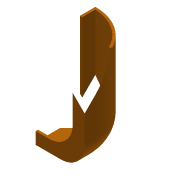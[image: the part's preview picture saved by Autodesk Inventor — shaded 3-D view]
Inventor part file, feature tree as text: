
AUTODESK INVENTOR PART (.ipt)
format: ipt  version: 2016 (Build 200138000, 138)  size: 146,432 bytes
history: native  units: mm
features: plane x4, sketch x3, extrude x3, reference x2, fillet x1, projected_geometry x1
ambient origin geometry x8: Origin, YZ Plane, XZ Plane, XY Plane, X Axis, Y Axis, Z Axis, Center Point
bodies: Body1 (feature_tree)
feature tree (14):
  sketch  "Sketch1"  dims[d1=2.0mm d2=2.0mm]
  plane  "Work Plane1"
  plane  "Work Plane2"
  plane  "Work Plane3"
  plane  "Work Plane4"
  extrude  "Extrusion2"  Depth=2.0mm
  extrude  "Extrusion3"  Depth=2.0mm
  extrude  "Extrusion4"  Depth=2.0mm TaperAngle=0.0deg
  fillet  "Fillet1"  Radius=8.0mm
  reference  "Reference1"
  reference  "Reference2"
  sketch  "Sketch2"  dims[d3=13.0mm d6=2.0mm]
  sketch  "Sketch3"  dims[d7=10.0mm d8=0.0mm d9=2.0mm d10=0.0mm d11=8.0mm d12=8.0mm d13=2.0mm d14=0.0mm d15=20.0mm]
  projected_geometry  "Projected Loop1"
